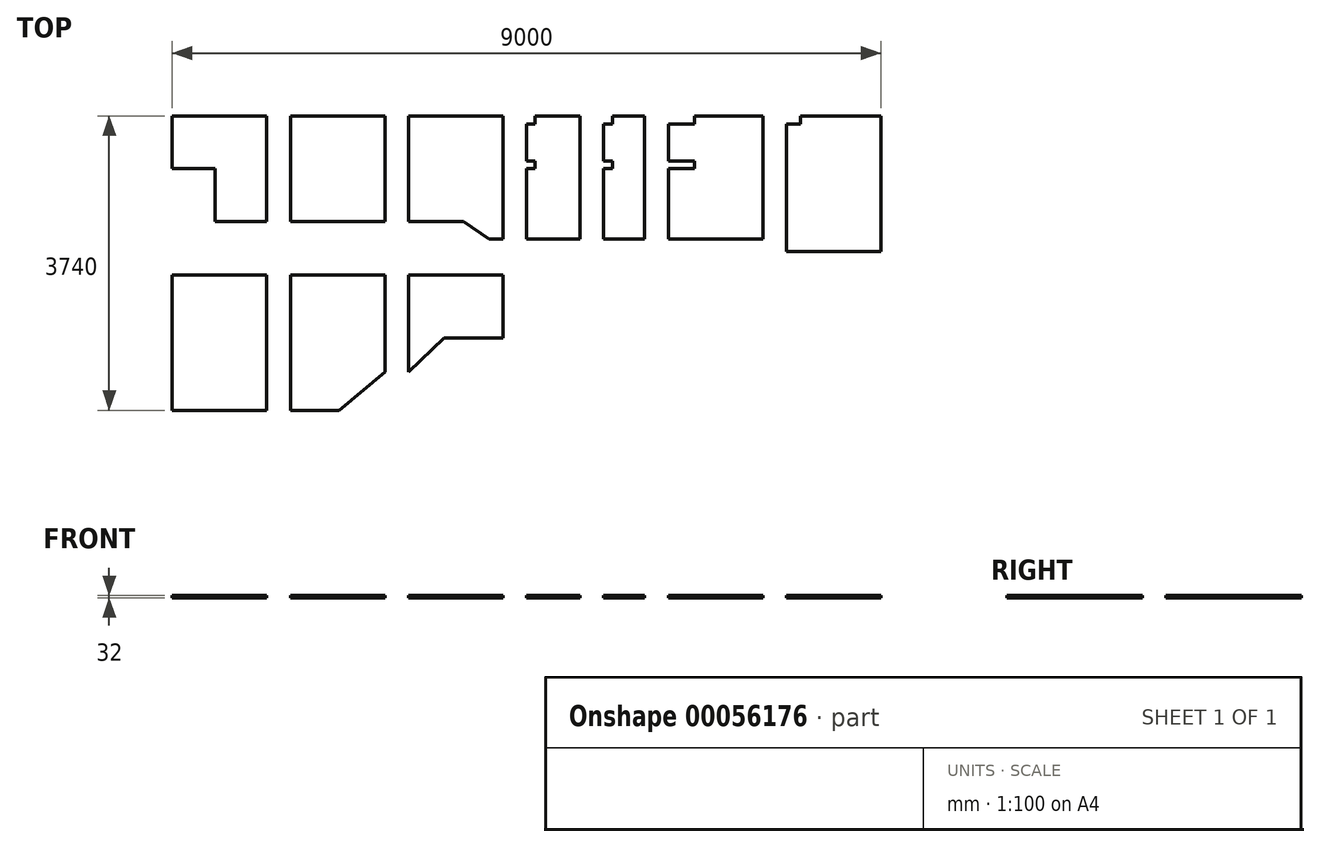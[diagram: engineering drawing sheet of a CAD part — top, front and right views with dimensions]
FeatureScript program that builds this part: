
annotation { "Feature Type Name" : "Feature", "Feature Type Description" : "" }
export const myFeature = defineFeature(function(context is Context, id is Id, definition is map)
    precondition{}
    {
        {
            var Q0;
            Q0=qCreatedBy(makeId("Top.planeOp"),FACE);
            var sketch = newSketch(context, id + "F0", { "sketchPlane" : qUnion([Q0])});
            skLineSegment(sketch, "E0.bottom", {"start": v(-760.54, 1104.3) * mm, "end": v(439.46, 1104.3) * mm});
            skLineSegment(sketch, "E0.top", {"start": v(-220.54, -235.7) * mm, "end": v(439.46, -235.7) * mm});
            skLineSegment(sketch, "E0.left", {"start": v(-760.54, 1104.3) * mm, "end": v(-760.54, 434.3) * mm});
            skLineSegment(sketch, "E0.right", {"start": v(439.46, 1104.3) * mm, "end": v(439.46, -235.7) * mm});
            skLineSegment(sketch, "E1.bottom", {"start": v(-760.54, 434.3) * mm, "end": v(-220.54, 434.3) * mm});
            skLineSegment(sketch, "E1.right", {"start": v(-220.54, 434.3) * mm, "end": v(-220.54, -235.7) * mm});
            skLineSegment(sketch, "E2.bottom", {"start": v(739.46, 1104.3) * mm, "end": v(1939.46, 1104.3) * mm});
            skLineSegment(sketch, "E2.top", {"start": v(739.46, -235.7) * mm, "end": v(1939.46, -235.7) * mm});
            skLineSegment(sketch, "E2.left", {"start": v(739.46, 1104.3) * mm, "end": v(739.46, -235.7) * mm});
            skLineSegment(sketch, "E2.right", {"start": v(1939.46, 1104.3) * mm, "end": v(1939.46, -235.7) * mm});
            skLineSegment(sketch, "E3.bottom", {"start": v(2239.46, 1104.3) * mm, "end": v(3439.46, 1104.3) * mm});
            skLineSegment(sketch, "E3.top", {"start": v(3259.46, -455.7) * mm, "end": v(3439.46, -455.7) * mm});
            skLineSegment(sketch, "E3.left", {"start": v(2239.46, 1104.3) * mm, "end": v(2239.46, -235.7) * mm});
            skLineSegment(sketch, "E3.right", {"start": v(3439.46, 1104.3) * mm, "end": v(3439.46, -455.7) * mm});
            skLineSegment(sketch, "E4", {"start": v(2239.46, -235.7) * mm, "end": v(2939.46, -235.7) * mm});
            skLineSegment(sketch, "E5", {"start": v(2939.46, -235.7) * mm, "end": v(3259.46, -455.7) * mm});
            skLineSegment(sketch, "E6.bottom", {"start": v(3849.46, 1104.3) * mm, "end": v(4419.46, 1104.3) * mm});
            skLineSegment(sketch, "E6.top", {"start": v(3739.46, -455.7) * mm, "end": v(4419.46, -455.7) * mm});
            skLineSegment(sketch, "E6.left", {"start": v(3739.46, 1004.3) * mm, "end": v(3739.46, 534.3) * mm});
            skLineSegment(sketch, "E6.right", {"start": v(4419.46, 1104.3) * mm, "end": v(4419.46, -455.7) * mm});
            skLineSegment(sketch, "E7.top", {"start": v(3739.46, 1004.3) * mm, "end": v(3849.46, 1004.3) * mm});
            skLineSegment(sketch, "E7.right", {"start": v(3849.46, 1104.3) * mm, "end": v(3849.46, 1004.3) * mm});
            skLineSegment(sketch, "E8.bottom", {"start": v(3739.46, 534.3) * mm, "end": v(3849.46, 534.3) * mm});
            skLineSegment(sketch, "E8.top", {"start": v(3739.46, 434.3) * mm, "end": v(3849.46, 434.3) * mm});
            skLineSegment(sketch, "E8.right", {"start": v(3849.46, 534.3) * mm, "end": v(3849.46, 434.3) * mm});
            skLineSegment(sketch, "E9.trimOffspring", {"start": v(3739.46, 434.3) * mm, "end": v(3739.46, -455.7) * mm});
            skLineSegment(sketch, "E10.top", {"start": v(4719.46, 1004.3) * mm, "end": v(4829.46, 1004.3) * mm});
            skLineSegment(sketch, "E11.bottom", {"start": v(4719.46, 534.3) * mm, "end": v(4829.46, 534.3) * mm});
            skLineSegment(sketch, "E12.left", {"start": v(4719.46, 1004.3) * mm, "end": v(4719.46, 534.3) * mm});
            skLineSegment(sketch, "E11.top", {"start": v(4719.46, 434.3) * mm, "end": v(4829.46, 434.3) * mm});
            skLineSegment(sketch, "E13.trimOffspring", {"start": v(4719.46, 434.3) * mm, "end": v(4719.46, -455.7) * mm});
            skLineSegment(sketch, "E12.top", {"start": v(4719.46, -455.7) * mm, "end": v(5239.46, -455.7) * mm});
            skLineSegment(sketch, "E12.right", {"start": v(5239.46, 1104.3) * mm, "end": v(5239.46, -455.7) * mm});
            skLineSegment(sketch, "E12.bottom", {"start": v(4829.46, 1104.3) * mm, "end": v(5239.46, 1104.3) * mm});
            skLineSegment(sketch, "E10.right", {"start": v(4829.46, 1104.3) * mm, "end": v(4829.46, 1004.3) * mm});
            skLineSegment(sketch, "E11.right", {"start": v(4829.46, 534.3) * mm, "end": v(4829.46, 434.3) * mm});
            skLineSegment(sketch, "E14.top", {"start": v(5539.46, 1004.3) * mm, "end": v(5869.46, 1004.3) * mm});
            skLineSegment(sketch, "E15.bottom", {"start": v(5539.46, 534.3) * mm, "end": v(5869.46, 534.3) * mm});
            skLineSegment(sketch, "E16.left", {"start": v(5539.46, 1004.3) * mm, "end": v(5539.46, 534.3) * mm});
            skLineSegment(sketch, "E15.top", {"start": v(5539.46, 434.3) * mm, "end": v(5869.46, 434.3) * mm});
            skLineSegment(sketch, "E17.trimOffspring", {"start": v(5539.46, 434.3) * mm, "end": v(5539.46, -455.7) * mm});
            skLineSegment(sketch, "E16.top", {"start": v(5539.46, -455.7) * mm, "end": v(6739.46, -455.7) * mm});
            skLineSegment(sketch, "E16.right", {"start": v(6739.46, 1104.3) * mm, "end": v(6739.46, -455.7) * mm});
            skLineSegment(sketch, "E16.bottom", {"start": v(5869.46, 1104.3) * mm, "end": v(6739.46, 1104.3) * mm});
            skLineSegment(sketch, "E14.right", {"start": v(5869.46, 1104.3) * mm, "end": v(5869.46, 1004.3) * mm});
            skLineSegment(sketch, "E15.right", {"start": v(5869.46, 534.3) * mm, "end": v(5869.46, 434.3) * mm});
            skLineSegment(sketch, "E18.top", {"start": v(7039.46, 1004.3) * mm, "end": v(7219.46, 1004.3) * mm});
            skLineSegment(sketch, "E19.left", {"start": v(7039.46, 1004.3) * mm, "end": v(7039.46, 407.84) * mm});
            skLineSegment(sketch, "E20.trimOffspring", {"start": v(7039.46, 307.84) * mm, "end": v(7039.46, -615.7) * mm});
            skLineSegment(sketch, "E19.top", {"start": v(7039.46, -615.7) * mm, "end": v(8239.46, -615.7) * mm});
            skLineSegment(sketch, "E19.right", {"start": v(8239.46, 1104.3) * mm, "end": v(8239.46, -615.7) * mm});
            skLineSegment(sketch, "E19.bottom", {"start": v(7219.46, 1104.3) * mm, "end": v(8239.46, 1104.3) * mm});
            skLineSegment(sketch, "E18.right", {"start": v(7219.46, 1104.3) * mm, "end": v(7219.46, 1004.3) * mm});
            skLineSegment(sketch, "E21", {"start": v(7039.46, 407.84) * mm, "end": v(7039.46, 307.84) * mm});
            skLineSegment(sketch, "E22.bottom", {"start": v(-760.54, -915.7) * mm, "end": v(439.46, -915.7) * mm});
            skLineSegment(sketch, "E22.top", {"start": v(-760.54, -2635.7) * mm, "end": v(439.46, -2635.7) * mm});
            skLineSegment(sketch, "E22.left", {"start": v(-760.54, -915.7) * mm, "end": v(-760.54, -2635.7) * mm});
            skLineSegment(sketch, "E22.right", {"start": v(439.46, -915.7) * mm, "end": v(439.46, -2635.7) * mm});
            skLineSegment(sketch, "E23.bottom", {"start": v(739.46, -915.7) * mm, "end": v(1939.46, -915.7) * mm});
            skLineSegment(sketch, "E23.top", {"start": v(739.46, -2635.7) * mm, "end": v(1359.46, -2635.7) * mm});
            skLineSegment(sketch, "E23.left", {"start": v(739.46, -915.7) * mm, "end": v(739.46, -2635.7) * mm});
            skLineSegment(sketch, "E23.right", {"start": v(1939.46, -915.7) * mm, "end": v(1939.46, -2145.7) * mm});
            skLineSegment(sketch, "E24", {"start": v(1359.46, -2635.7) * mm, "end": v(1939.46, -2145.7) * mm});
            skLineSegment(sketch, "E25.bottom", {"start": v(2239.46, -915.7) * mm, "end": v(3439.46, -915.7) * mm});
            skLineSegment(sketch, "E25.left", {"start": v(2239.46, -915.7) * mm, "end": v(2239.46, -2145.7) * mm});
            skLineSegment(sketch, "E25.right", {"start": v(3439.46, -915.7) * mm, "end": v(3439.46, -1715.7) * mm});
            skLineSegment(sketch, "E26", {"start": v(3439.46, -1715.7) * mm, "end": v(2689.46, -1715.7) * mm});
            skLineSegment(sketch, "E27", {"start": v(2689.46, -1715.7) * mm, "end": v(2239.46, -2145.7) * mm});
            skSolve(sketch);
        }
        {
            var Q0;
            Q0 = qSketchRegion(id + "F0", true);
            extrude(context, id + "F1", {"entities" : qUnion([Q0]), "depth" : 32 * mm});
        }
    });
